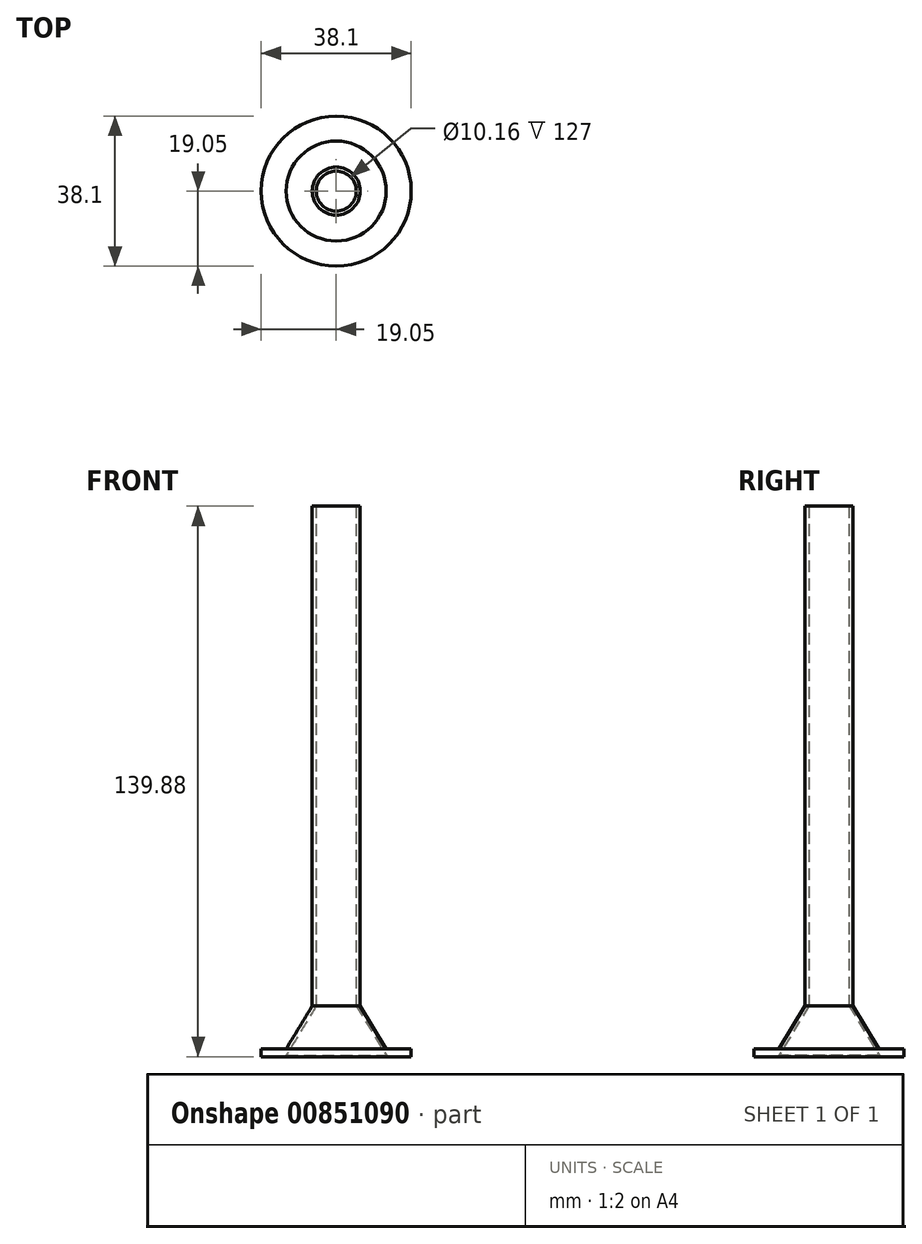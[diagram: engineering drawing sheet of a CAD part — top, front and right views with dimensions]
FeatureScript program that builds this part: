
annotation { "Feature Type Name" : "Feature", "Feature Type Description" : "" }
export const myFeature = defineFeature(function(context is Context, id is Id, definition is map)
    precondition{}
    {
        {
            var Q0;
            Q0=qCreatedBy(makeId("Front.planeOp"),FACE);
            var sketch = newSketch(context, id + "F0", { "sketchPlane" : qUnion([Q0])});
            skLineSegment(sketch, "E0", {"start": v(-12.7, 9.45) * mm, "end": v(-19.05, 9.45) * mm});
            skLineSegment(sketch, "E1", {"start": v(-19.05, 9.45) * mm, "end": v(-19.05, 11.49) * mm});
            skLineSegment(sketch, "E2", {"start": v(-19.05, 11.49) * mm, "end": v(-12.7, 11.49) * mm});
            skLineSegment(sketch, "E3", {"start": v(-12.7, 11.49) * mm, "end": v(-6.1, 22.33) * mm});
            skLineSegment(sketch, "E4", {"start": v(-6.1, 22.33) * mm, "end": v(-6.1, 149.33) * mm});
            skLineSegment(sketch, "E5", {"start": v(-6.1, 149.33) * mm, "end": v(-5.08, 149.33) * mm});
            skLineSegment(sketch, "E6", {"start": v(-5.08, 149.33) * mm, "end": v(-5.08, 22.33) * mm});
            skLineSegment(sketch, "E7", {"start": v(0, 0) * mm, "end": v(0, 160.64) * mm, "construction": true});
            skLineSegment(sketch, "E8", {"start": v(-5.08, 22.33) * mm, "end": v(-12.72, 9.78) * mm});
            skLineSegment(sketch, "E9", {"start": v(-12.72, 9.78) * mm, "end": v(-12.7, 9.45) * mm});
            skSolve(sketch);
        }
        {
            var Q0;
            Q0 = qSketchRegion(id + "F0", true);
            var Q1;
            Q1=sQuery(id+"F0.wireOp",EDGE,"E7");
            revolve(context, id + "F1", {"surfaceOperationType" : NewSurfaceOperationType.NEW, "entities" : qUnion([Q0]), "axis" : qUnion([Q1]), "revolveType" : RevolveType.FULL});
        }
    });
